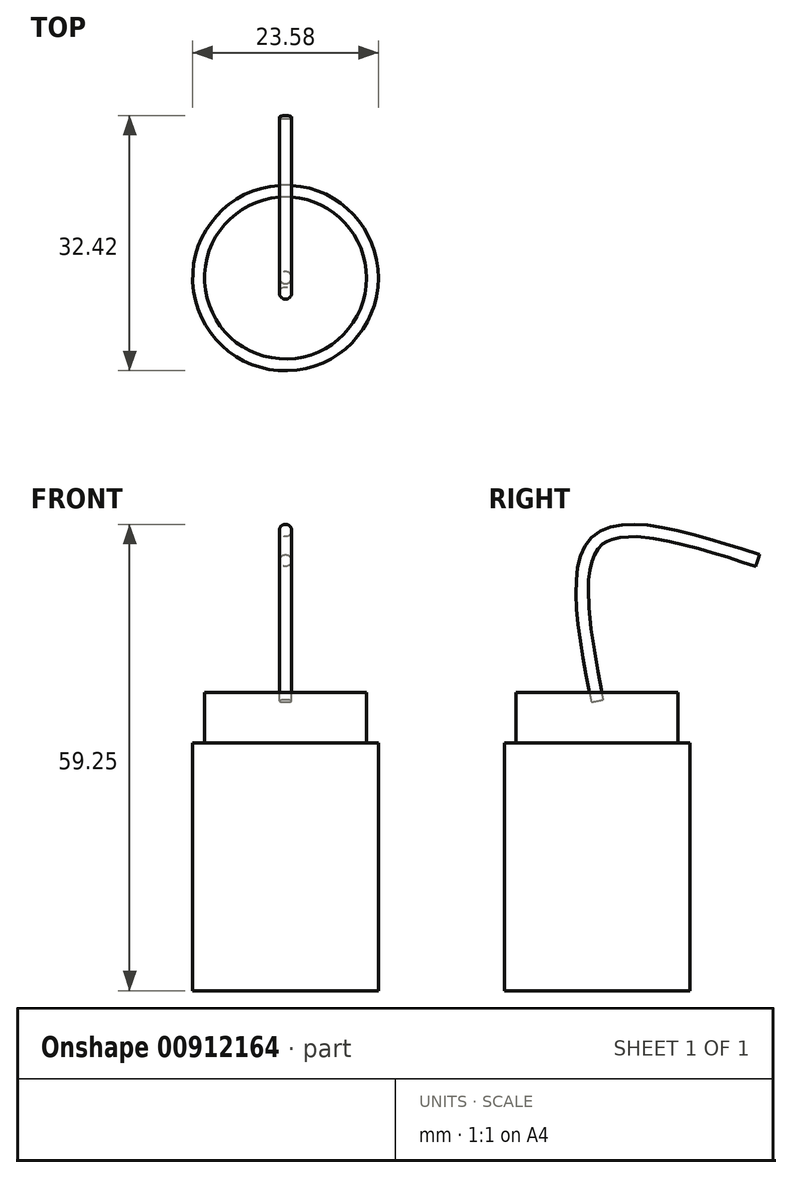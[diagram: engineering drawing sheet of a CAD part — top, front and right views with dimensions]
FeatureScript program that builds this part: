
annotation { "Feature Type Name" : "Feature", "Feature Type Description" : "" }
export const myFeature = defineFeature(function(context is Context, id is Id, definition is map)
    precondition{}
    {
        {
            var Q0;
            Q0=qCreatedBy(makeId("Top.planeOp"),FACE);
            var sketch = newSketch(context, id + "F0", { "sketchPlane" : qUnion([Q0])});
            skCircle(sketch, "E0", {"center": v(0, 0) * mm, "radius": 11.8 * mm});
            skSolve(sketch);
        }
        {
            var Q0;
            Q0 = qSketchRegion(id + "F0", true);
            extrude(context, id + "F1", {"entities" : qUnion([Q0]), "depth" : 31.5 * mm, "offsetDistance" : 25.4 * mm});
        }
        {
            var Q0;
            Q0=makeQuery(id+"F1.opExtrude","CAP_FACE",FACE,{"disambiguationData":[OSD([sQuery(id+"F0.wireOp",EDGE,"E0")])],"isStart":false});
            var sketch = newSketch(context, id + "F2", { "sketchPlane" : qUnion([Q0])});
            skCircle(sketch, "E1", {"center": v(0, 0) * mm, "radius": 10.3 * mm});
            skSolve(sketch);
        }
        {
            var Q0;
            Q0 = qSketchRegion(id + "F2", true);
            extrude(context, id + "F3", {"entities" : qUnion([Q0]), "operationType" : NewBodyOperationType.ADD, "depth" : 6.4 * mm, "offsetDistance" : 25.4 * mm});
        }
        {
            var Q0;
            Q0=qCreatedBy(makeId("Right.planeOp"),FACE);
            var sketch = newSketch(context, id + "F4", { "sketchPlane" : qUnion([Q0])});
            skFitSpline(sketch, "E2", {"points": [v(0, 36.8) * mm, v(0, 57.2) * mm, v(20.4, 54.68) * mm], "startDerivative": vector(-10.16, 52.36) * mm, "endDerivative": vector(50.93, -16.54) * mm});
            skSolve(sketch);
        }
        {
            var Q0;
            Q0=sQuery(id+"F4.wireOp",VERTEX,"E2.end");
            var Q1;
            Q1=sQuery(id+"F4.wireOp",EDGE,"E2");
            cPlane(context, id + "F5", {"entities" : qUnion([Q0, Q1]), "cplaneType" : CPlaneType.CURVE_POINT, "offset" : 25.4 * mm, "width" : 152.4 * mm, "height" : 152.4 * mm});
        }
        {
            var Q0;
            Q0=qCreatedBy(id+"F5.planeOp",FACE);
            var sketch = newSketch(context, id + "F6", { "sketchPlane" : qUnion([Q0])});
            skCircle(sketch, "E3", {"center": v(0, 58.27) * mm, "radius": 0.78 * mm});
            skSolve(sketch);
        }
        {
            var Q0;
            Q0 = qSketchRegion(id + "F6", true);
            var Q1;
            Q1 = qConstructionFilter(qBodyType(qCreatedBy(id + "F4" ,EDGE), BodyType.WIRE), ConstructionObject.NO);
            sweep(context, id + "F7", {"profiles" : qUnion([Q0]), "path" : qUnion([Q1])});
        }
    });
